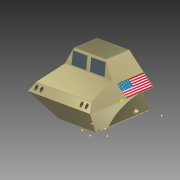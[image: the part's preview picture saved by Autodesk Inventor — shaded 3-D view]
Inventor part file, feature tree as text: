
AUTODESK INVENTOR PART (.ipt)
format: ipt  version: 2015 (Build 190159000, 159)  size: 418,304 bytes
history: native  units: in
note: dims shown in document units (in); Inventor stores cm internally (conversion verified against a paired STEP export)
features: sketch x23, extrude x11, plane x7, mirror x5, chamfer x4, other x3, projected_geometry x3, fillet x1, hole x1
ambient origin geometry x8: Origin, YZ Plane, XZ Plane, XY Plane, X Axis, Y Axis, Z Axis, Center Point
bodies: Solid1 (feature_tree)
feature tree (58):
  extrude  "Extrusion1"  Depth=3.06in
  extrude  "Extrusion2"  Depth=0.5in
  chamfer  "Chamfer1"  Distance=2.625in
  chamfer  "Chamfer2"  Distance=1.625in Angle=45.0deg
  extrude  "Extrusion3"  Depth=6.75in TaperAngle=0.0deg
  chamfer  "Chamfer3"  Distance=1.435in Angle=45.0deg
  chamfer  "Chamfer4"  Distance=1.435in Angle=45.0deg
  plane  "Work Plane1"
  extrude  "Extrusion4"  Depth=0.737in
  sketch  "Sketch5"  dims[d22=-1.38in d23=0.737in]
  plane  "Work Plane2"
  mirror  "Mirror1"
  extrude  "Extrusion5"  TaperAngle=90.0deg  [1 undecoded]
  mirror  "Mirror2"
  sketch  "Sketch7"  dims[d27=1.375in d28=1.375in d29=0.0in]
  sketch  "Sketch8"  dims[d30=1.516in d31=0.25in]
  sketch  "Sketch9"  dims[d32=0.36in d33=0.4in d34=0.0in d44=0.68in]
  other  "Work Point1"
  mirror  "Mirror3"
  plane  "Work Plane4"
  plane  "Work Plane5"
  plane  "Work Plane6"
  sketch  "Sketch10"  dims[d45=0.68in d51=0.05in d52=0.0in]
  sketch  "Sketch11"  dims[d53=2.4in d54=0.93in]
  sketch  "Sketch12"  dims[d55=0.795in d56=1.065in]
  sketch  "Sketch13"  dims[d57=0.57in d58=0.0in d59=0.2in]
  extrude  "Extrusion6"  Depth=1.375in TaperAngle=0.0deg
  mirror  "Mirror4"
  sketch  "Sketch15"  dims[d83=0.307in d84=0.75in d85=0.375in d86=0.25in d87=0.5635in d88=0.4in d89=0.8108in]
  extrude  "Extrusion7"  Depth=0.25in
  extrude  "Extrusion8"  Depth=0.4in TaperAngle=0.0deg
  fillet  "Fillet1"  Radius=0.68in
  plane  "Work Plane7"
  sketch  "Sketch18"  dims[d62=1.0in]
  extrude  "Extrusion9"  Depth=0.05in TaperAngle=0.0deg
  sketch  "Sketch20"  dims[d69=1.0in]
  hole  "Hole4"  [1 undecoded]
  mirror  "Mirror6"
  extrude  "Extrusion10"  Depth=1.065in
  extrude  "Extrusion11"  Depth=0.2in
  sketch  "Sketch1"  dims[d0=3.17in d1=3.06in]
  sketch  "Sketch2"  dims[d2=6.75in d3=0.0in d4=0.5in]
  sketch  "Sketch3"  dims[d5=0.5in d6=2.625in d7=0.0in d8=1.625in d9=0.125in d10=45.0deg]
  sketch  "Sketch4"  dims[d11=1.625in d12=0.125in d13=45.0deg d14=6.75in d15=0.0in d16=1.435in d17=0.125in d18=45.0deg d19=1.435in d20=0.125in d21=45.0deg]
  projected_geometry  "Projected Loop1"
  plane  "Work Plane3"
  sketch  "Sketch6"  dims[d24=1.375in d25=0.0in d26=90.0deg]
  other  "Work Point2"
  sketch  "Sketch14"  dims[d60=0.05in d61=0.0in]
  other  "Image1"
  sketch  "Sketch16"  dims[d90=1.0in d91=0.0in]
  sketch  "Sketch17"  dims[d92=1.0in d93=0.0in]
  sketch  "Sketch19"  dims[d63=1.0in]
  sketch  "Sketch24"  dims[d70=1.0in]
  sketch  "Sketch25"
  projected_geometry  "Projected Loop2"
  sketch  "Sketch26"
  projected_geometry  "Projected Loop3"
note: 2 required parameter values undecoded (feature->parameter linkage not recoverable at this tier; creation-order binding heuristic only, values carry confidence <= 0.55)
